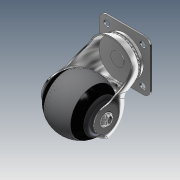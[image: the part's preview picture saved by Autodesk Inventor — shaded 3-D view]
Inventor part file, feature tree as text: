
AUTODESK INVENTOR PART (.ipt)
format: ipt  version: 2014 SP2 (Build 180246200, 246)  size: 689,152 bytes
history: native  units: mm
features: sketch x14, extrude x7, fillet x6, revolve x5, other x4, plane x2, hole x1, mirror x1, pattern_circular x1, shell x1
ambient origin geometry x8: Origin, YZ Plane, XZ Plane, XY Plane, X Axis, Y Axis, Z Axis, Center Point
bodies: Body1 (feature_tree), Body2 (feature_tree), Body3 (feature_tree), Body4 (feature_tree)
feature tree (42):
  other  "Sólido1"
  extrude  "Extrusión1"  Depth=1.2mm TaperAngle=0.0deg
  hole  "Hole1"  [1 undecoded]
  fillet  "Empalme1"  Radius=28.0mm
  extrude  "Extrusión2"  Depth=35.0mm
  sketch  "Boceto5"  dims[d13=2.5mm d14=15.0deg d15=35.0mm]
  plane  "Plano de trabajo1"
  revolve  "Revolución1"  Angle=90.0deg
  fillet  "Empalme2"  Radius=5.0mm
  extrude  "Extrusión3"  Depth=5.0mm TaperAngle=0.0deg
  mirror  "Simetría1"
  revolve  "Revolución2"  [1 undecoded]
  sketch  "Boceto9"  dims[d27=21.35mm d31=90.0deg]
  revolve  "Revolución3"  Angle=90.0deg
  sketch  "Boceto21"  dims[d72=3.0mm d73=90.0deg d74=300.0mm d75=360.0deg d84=1.0mm d86=5.0mm d89=90.0deg d92=5.0mm d93=8.718707mm d94=1.0mm d95=100.0mm d96=0.0mm d97=5.0mm]
  extrude  "Extrusión5"  Depth=15.0mm
  fillet  "Empalme4"  Radius=23.151175mm
  extrude  "Extrusión6"  Depth=20.0mm
  fillet  "Empalme5"  Radius=2.0mm
  extrude  "Extrusión7"  Depth=10.0mm TaperAngle=0.0deg
  plane  "Plano de trabajo5"
  revolve  "Revolución5"  [1 undecoded]
  pattern_circular  "Patrón circular1"  Angle=90.0deg  [1 undecoded]
  revolve  "Revolución6"  Angle=360.0deg
  fillet  "Empalme6"  Radius=1.0mm
  sketch  "Boceto14"  dims[d35=19.25mm d37=15.0mm d38=23.151175mm]
  shell  "Vaciado1"  Thickness=5.0mm
  extrude  "Extrusión10"  TaperAngle=90.0deg  [1 undecoded]
  fillet  "Empalme7"  Radius=5.0mm
  sketch  "Boceto1"  dims[d0=38.0mm d1=1.2mm d2=0.0mm]
  sketch  "Boceto2"  dims[d3=27.0mm]
  sketch  "Boceto4"  dims[d4=4.5mm d5=6.0mm d6=4.0mm d7=2.0mm d8=90.0deg d9=8.0mm d10=20.594885mm d11=5.0mm d12=28.0mm]
  sketch  "Boceto6"  dims[d16=-35.0mm d19=90.0deg d20=5.0mm]
  sketch  "Boceto7"  dims[d21=4.9mm d22=5.0mm d23=0.0mm]
  sketch  "Boceto8"  dims[d25=90.0deg d26=21.30204mm]
  other  "Sólido2"
  other  "Sólido3"
  other  "Sólido4"
  sketch  "Boceto16"  dims[d61=20.0mm d62=1.0mm d63=-8.726646mm d64=2.0mm]
  sketch  "Boceto17"  dims[d65=10.0mm d66=1.0mm d67=0.0mm]
  sketch  "Boceto18"  dims[d68=0.5mm d69=5.75mm d70=0.0mm]
  sketch  "Boceto19"  dims[d71=0.75mm]
note: 5 required parameter values undecoded (feature->parameter linkage not recoverable at this tier; creation-order binding heuristic only, values carry confidence <= 0.55)